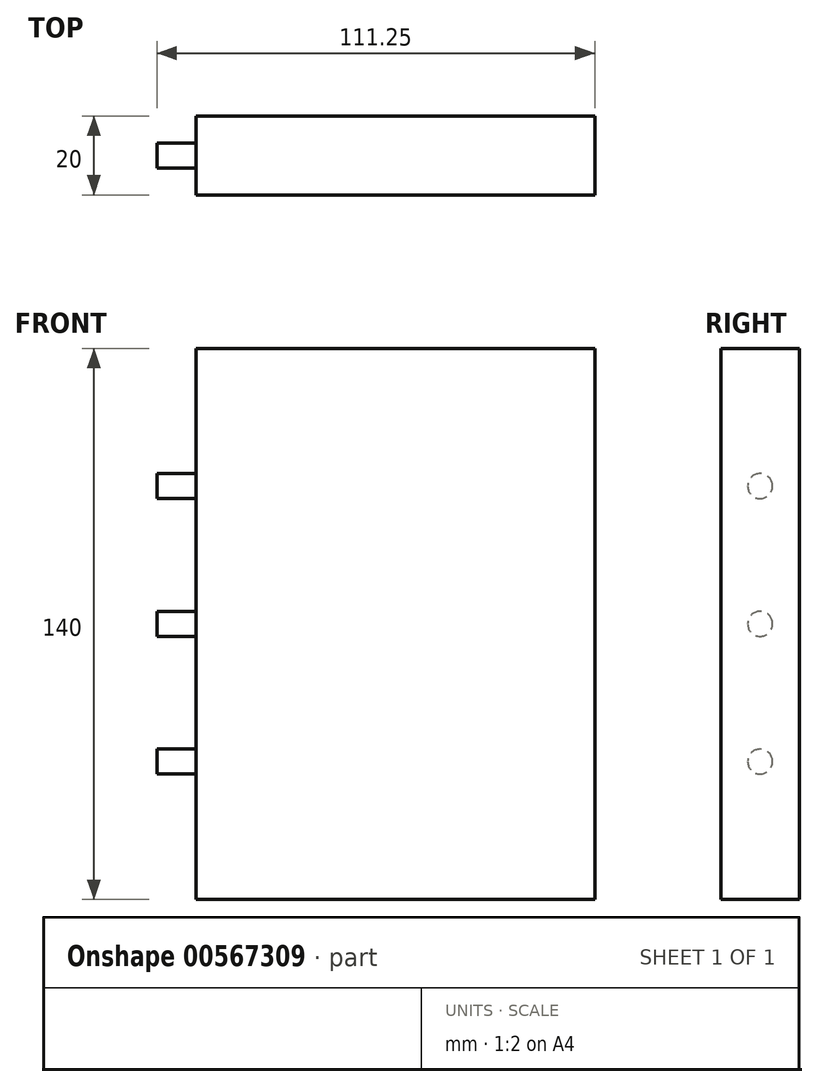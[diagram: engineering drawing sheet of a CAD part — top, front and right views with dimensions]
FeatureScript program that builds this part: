
annotation { "Feature Type Name" : "Feature", "Feature Type Description" : "" }
export const myFeature = defineFeature(function(context is Context, id is Id, definition is map)
    precondition{}
    {
        {
            var Q0;
            Q0=qCreatedBy(makeId("Front.planeOp"),FACE);
            var sketch = newSketch(context, id + "F0", { "sketchPlane" : qUnion([Q0])});
            skLineSegment(sketch, "E0.bottom", {"start": v(70, 70) * mm, "end": v(-70, 70) * mm});
            skLineSegment(sketch, "E0.top", {"start": v(70, -70) * mm, "end": v(-70, -70) * mm});
            skLineSegment(sketch, "E0.left", {"start": v(70, 70) * mm, "end": v(70, -70) * mm});
            skLineSegment(sketch, "E0.right", {"start": v(-70, 70) * mm, "end": v(-70, -70) * mm});
            skPoint(sketch, "E0.middle", {"position": v(0, 0) * mm});
            skSolve(sketch);
        }
        {
            var Q0;
            Q0 = qSketchRegion(id + "F0", true);
            var Q1;
            Q1=makeQuery(id+"F0.imprint","IMPRINT",FACE,{"disambiguationData":[TD([[makeQuery(id+"F0.imprint","IMPRINT",EDGE,{"derivedFrom":sQuery(id+"F0.wireOp",EDGE,"E0.bottom")}),1.0]])]});
            extrude(context, id + "F1", {"entities" : qUnion([Q0, Q1]), "depth" : 20 * mm, "offsetDistance" : 25.4 * mm});
        }
        {
            var Q0;
            Q0=makeQuery(id+"F1.opExtrude","SWEPT_FACE",FACE,{"disambiguationData":[OSD([sQuery(id+"F0.wireOp",EDGE,"E0.right")])]});
            var sketch = newSketch(context, id + "F2", { "sketchPlane" : qUnion([Q0])});
            skLineSegment(sketch, "E1", {"start": v(0, 0) * mm, "end": v(20, 0) * mm});
            skLineSegment(sketch, "E2", {"start": v(20, 0) * mm, "end": v(20, 35) * mm});
            skLineSegment(sketch, "E3", {"start": v(20, 35) * mm, "end": v(0, 35) * mm});
            skLineSegment(sketch, "E4", {"start": v(20, 0) * mm, "end": v(20, -35) * mm});
            skLineSegment(sketch, "E5", {"start": v(20, -35) * mm, "end": v(0, -35) * mm});
            skCircle(sketch, "E6", {"center": v(10, -35) * mm, "radius": 3.18 * mm});
            skCircle(sketch, "E7", {"center": v(10, 0) * mm, "radius": 3.18 * mm});
            skCircle(sketch, "E8", {"center": v(10, 35) * mm, "radius": 3.18 * mm});
            skSolve(sketch);
        }
        {
            var Q0;
            {var subQ0=sQuery(id+"F2.wireOp",EDGE,"E8");var subQ1=sQuery(id+"F2.wireOp",EDGE,"E3");var subQ2=makeQuery(id+"F2.imprint","INTERSECT",VERTEX,{"disambiguationData":[OD(0.0)],"derivedFrom":[subQ1,subQ0]});Q0=makeQuery(id+"F2.imprint","IMPRINT",FACE,{"disambiguationData":[TD([[makeQuery(id+"F2.imprint","IMPRINT",EDGE,{"disambiguationData":[TD([[subQ2,-1.0]])],"derivedFrom":subQ1}),-1.0]])]});}
            var Q1;
            {var subQ0=sQuery(id+"F2.wireOp",EDGE,"E8");var subQ1=sQuery(id+"F2.wireOp",EDGE,"E3");var subQ2=makeQuery(id+"F2.imprint","INTERSECT",VERTEX,{"disambiguationData":[OD(0.0)],"derivedFrom":[subQ1,subQ0]});Q1=makeQuery(id+"F2.imprint","IMPRINT",FACE,{"disambiguationData":[TD([[makeQuery(id+"F2.imprint","IMPRINT",EDGE,{"disambiguationData":[TD([[subQ2,-1.0]])],"derivedFrom":subQ1}),1.0]])]});}
            var Q2;
            {var subQ0=sQuery(id+"F2.wireOp",EDGE,"E7");var subQ1=sQuery(id+"F2.wireOp",EDGE,"E1");var subQ2=makeQuery(id+"F2.imprint","INTERSECT",VERTEX,{"disambiguationData":[OD(0.0)],"derivedFrom":[subQ1,subQ0]});Q2=makeQuery(id+"F2.imprint","IMPRINT",FACE,{"disambiguationData":[TD([[makeQuery(id+"F2.imprint","IMPRINT",EDGE,{"disambiguationData":[TD([[subQ2,-1.0]])],"derivedFrom":subQ1}),1.0]])]});}
            var Q3;
            {var subQ0=sQuery(id+"F2.wireOp",EDGE,"E7");var subQ1=sQuery(id+"F2.wireOp",EDGE,"E1");var subQ2=makeQuery(id+"F2.imprint","INTERSECT",VERTEX,{"disambiguationData":[OD(0.0)],"derivedFrom":[subQ1,subQ0]});Q3=makeQuery(id+"F2.imprint","IMPRINT",FACE,{"disambiguationData":[TD([[makeQuery(id+"F2.imprint","IMPRINT",EDGE,{"disambiguationData":[TD([[subQ2,-1.0]])],"derivedFrom":subQ1}),-1.0]])]});}
            var Q4;
            {var subQ0=sQuery(id+"F2.wireOp",EDGE,"E6");var subQ1=sQuery(id+"F2.wireOp",EDGE,"E5");var subQ2=makeQuery(id+"F2.imprint","INTERSECT",VERTEX,{"disambiguationData":[OD(0.0)],"derivedFrom":[subQ1,subQ0]});Q4=makeQuery(id+"F2.imprint","IMPRINT",FACE,{"disambiguationData":[TD([[makeQuery(id+"F2.imprint","IMPRINT",EDGE,{"disambiguationData":[TD([[subQ2,-1.0]])],"derivedFrom":subQ1}),-1.0]])]});}
            var Q5;
            {var subQ0=sQuery(id+"F2.wireOp",EDGE,"E6");var subQ1=sQuery(id+"F2.wireOp",EDGE,"E5");var subQ2=makeQuery(id+"F2.imprint","INTERSECT",VERTEX,{"disambiguationData":[OD(0.0)],"derivedFrom":[subQ1,subQ0]});Q5=makeQuery(id+"F2.imprint","IMPRINT",FACE,{"disambiguationData":[TD([[makeQuery(id+"F2.imprint","IMPRINT",EDGE,{"disambiguationData":[TD([[subQ2,-1.0]])],"derivedFrom":subQ1}),1.0]])]});}
            extrude(context, id + "F3", {"entities" : qUnion([Q0, Q1, Q2, Q3, Q4, Q5]), "operationType" : NewBodyOperationType.REMOVE, "oppositeDirection" : true, "depth" : 10 * mm, "offsetDistance" : 25.4 * mm});
        }
        {
            var Q0;
            Q0=makeQuery(id+"F1.opExtrude","SWEPT_FACE",FACE,{"disambiguationData":[OSD([sQuery(id+"F0.wireOp",EDGE,"E0.left")])]});
            extrude(context, id + "F4", {"entities" : qUnion([Q0]), "operationType" : NewBodyOperationType.REMOVE, "oppositeDirection" : true, "depth" : 28.75 * mm, "offsetDistance" : 25 * mm});
        }
        {
            var Q0;
            Q0=makeQuery(id+"F1.opExtrude","SWEPT_FACE",FACE,{"disambiguationData":[OSD([sQuery(id+"F0.wireOp",EDGE,"E0.bottom")])]});
            var sketch = newSketch(context, id + "F5", { "sketchPlane" : qUnion([Q0])});
            skLineSegment(sketch, "E9", {"start": v(41.25, 0) * mm, "end": v(31.25, 0) * mm});
            skLineSegment(sketch, "E10", {"start": v(31.25, 0) * mm, "end": v(31.25, -20) * mm});
            skLineSegment(sketch, "E11", {"start": v(31.25, -20) * mm, "end": v(-70, -20) * mm});
            skLineSegment(sketch, "E12", {"start": v(-70, -20) * mm, "end": v(-19.38, -20) * mm});
            skLineSegment(sketch, "E13", {"start": v(-19.38, -20) * mm, "end": v(-19.38, 0) * mm});
            skSolve(sketch);
        }
        {
            var Q0;
            Q0=makeQuery(id+"F1.opExtrude","SWEPT_FACE",FACE,{"disambiguationData":[OSD([sQuery(id+"F0.wireOp",EDGE,"E0.top")])]});
            var sketch = newSketch(context, id + "F6", { "sketchPlane" : qUnion([Q0])});
            skLineSegment(sketch, "E14", {"start": v(-19.38, 20) * mm, "end": v(-19.38, 0) * mm});
            skSolve(sketch);
        }
    });
